# Revit family: 600х550
name_source: partatom
category: Обобщенные модели
units: mm (PartAtom-declared; Revit-internal decimal feet)

## family parameters
Всегда вертикально = Да
Может служить основой для арматурных стержней = Нет
На основе рабочей плоскости = Нет
Общий = Нет
При загрузке вырезать с полостями = Нет
Размер круглого соединителя = Использовать диаметр
Тип детали = Нормальный
Точка расчета площади = Нет

## types (6) — shared parameters
ADSK_URL страницы изделия = https://www.ssd.ru
ADSK_Единица измерения = шт
ADSK_Завод-изготовитель = АО СВЯЗЬСТРОЙДЕТАЛЬ
ADSK_Материал обозначение = Серый RAL 7035
ADSK_Размер_Глубина = 550 мм
ADSK_Размер_Ширина = 600 мм

## per-type parameters (varying)
| type | ADSK_Код изделия | ADSK_Масса_Текст | ADSK_Наименование | ADSK_Размер_Высота | Высота_двери | Дверь |
| ШТ-НСрМ 9U (600x550) стеклянная дверь | 130411-00823 | 21,4 | Шкаф телекоммуникационный настенный разборный со съемными боковыми стенками 19”,9U(600x550), ШТ-НСрМ-9U-600-550-С дверь стекло ССД | 493 мм | 413 мм | Дверь_С |
| ШТ-НСрМ 9U (600x550) металлическая дверь | 130411-00828 | 20,8 | Шкаф телекоммуникационный настенный разборный со съемными боковыми стенками 19”,9U(600x550), ШТ-НСрМ-9U-600-550-М дверь металл ССД | 493 мм | 413 мм | Дверь_М |
| ШТ-НСрМ 12U (600x550) стеклянная дверь | 130411-00829 | 24,4 | Шкаф телекоммуникационный настенный разборный со съемными боковыми стенками 19”,12U(600x550), ШТ-НСрМ-12U-600-550-С дверь стекло ССД | 626 мм | 546 мм | Дверь_С |
| ШТ-НСрМ 12U (600x550) металлическая дверь | 130411-00830 | 23,6 | Шкаф телекоммуникационный настенный разборный со съемными боковыми стенками 19”,12U(600x550), ШТ-НСрМ-12U-600-550-М дверь металл ССД | 626 мм | 546 мм | Дверь_М |
| ШТ-НСрМ 15U (600x550) стеклянная дверь | 130411-00831 | 31,0 | Шкаф телекоммуникационный настенный разборный со съемными боковыми стенками 19”,15U(600x550), ШТ-НСрМ-15U-600-550-С дверь стекло ССД | 760 мм | 680 мм | Дверь_С |
| ШТ-НСрМ 15U (600x550) металлическая дверь | 130411-00832 | 30,0 | Шкаф телекоммуникационный настенный разборный со съемными боковыми стенками 19”,15U(600x550), ШТ-НСрМ-15U-600-550-М дверь металл ССД | 760 мм | 680 мм | Дверь_М |

note: column(s) folded — value = type name in every type: ADSK_Обозначение
